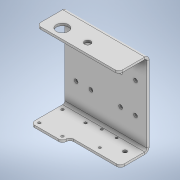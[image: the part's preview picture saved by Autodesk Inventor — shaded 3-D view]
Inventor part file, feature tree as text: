
AUTODESK INVENTOR PART (.ipt)
format: ipt  version: 2020 (Build 240168000, 168)  size: 329,216 bytes
history: native  units: in
note: dims shown in document units (in); Inventor stores cm internally (conversion verified against a paired STEP export)
features: sketch x9, hole x6, sheet_metal_op x3, other x2, chamfer x1
ambient origin geometry x8: Origin, YZ Plane, XZ Plane, XY Plane, X Axis, Y Axis, Z Axis, Center Point
bodies: Solid1 (feature_tree)
feature tree (21):
  sheet_metal_op  "Face1"
  sheet_metal_op  "Fold2"
  sheet_metal_op  "Fold3"
  hole  "Hole1"  [1 undecoded]
  hole  "Hole2"  [1 undecoded]
  chamfer  "Corner Round1"
  hole  "Hole4"  [1 undecoded]
  hole  "Hole5"  [1 undecoded]
  hole  "Hole6"  [1 undecoded]
  hole  "Hole7"  [1 undecoded]
  sketch  "Sketch2"  dims[d4=2.1654in d5=2.1654in]
  other  "Plate1"
  sketch  "Sketch4"  dims[d6=3.622in d7=7.5591in]
  sketch  "Sketch5"  dims[d8=0.1181in d17=2.126in]
  sketch  "Sketch6"  dims[d18=0.1181in d19=0.0591in]
  sketch  "Sketch7"  dims[d20=0.2362in d21=0.1181in]
  sketch  "Sketch9"  dims[d22=90.0deg d23=0.1181in d24=2.126in]
  sketch  "Sketch10"  dims[d25=0.1181in]
  sketch  "Sketch11"  dims[d26=0.0591in]
  sketch  "Sketch12"  dims[d27=0.2362in d28=0.1181in d29=90.0deg d30=0.1181in d31=0.8in d32=0.8in d33=0.2008in d35=0.7815in d37=0.2008in d38=0.2362in d39=0.1575in d40=0.0787in d41=90.0deg d42=0.1181in d43=0.8108in d44=0.7815in d45=0.2008in d46=0.2008in d47=1.5689in d48=1.5689in d49=0.2008in d50=0.2008in d51=0.2008in d52=0.2008in d53=0.7815in d54=1.5689in d55=1.5689in d56=0.7815in d57=0.2008in d61=0.3346in d62=0.0in d63=0.3228in d64=0.2362in d65=0.1575in d66=0.0787in d67=90.0deg d68=0.1181in d69=0.8108in d73=1.6654in d74=0.3937in d77=0.1969in d104=0.122in d105=0.122in d106=0.122in d107=1.1811in d108=1.5748in d109=0.2953in d110=1.1811in d111=1.378in d112=1.378in d113=0.122in d114=0.2362in d115=0.1575in d116=0.0787in d117=90.0deg d118=0.1181in d119=0.8108in d123=2.1654in d125=0.2008in d126=0.5413in d127=0.7874in d128=0.2008in d129=0.2362in d130=0.1575in d131=0.0787in d132=90.0deg d133=0.1181in d134=0.8108in d135=1.3327in d148=0.6378in d149=0.8327in d154=0.8327in d155=0.8327in d156=0.6378in d157=0.2362in d158=0.1575in d159=0.0787in d160=90.0deg d161=0.1181in d162=0.8108in d164=0.1654in d165=0.1654in d166=0.1654in d167=0.1654in d168=0.2224in d169=1.2205in d170=1.2205in d171=1.2205in d172=1.2205in d173=0.2224in d174=0.2224in d175=0.1378in d176=0.2362in d177=0.1575in d178=0.0787in d179=90.0deg d180=0.1181in d181=0.8108in d58=0.0394in d59=0.0394in d60=0.0394in d92=0.0394in d93=0.0394in d94=0.0394in d95=0.0059in d96=0.0098in d97=0.0148in d98=0.5635in d99=0.0295in d100=0.8108in d101=0.0025in d102=0.0295in d103=0.0148in d136=0.0148in]
  other  "Definition1"
note: 6 required parameter values undecoded (feature->parameter linkage not recoverable at this tier; creation-order binding heuristic only, values carry confidence <= 0.55)
